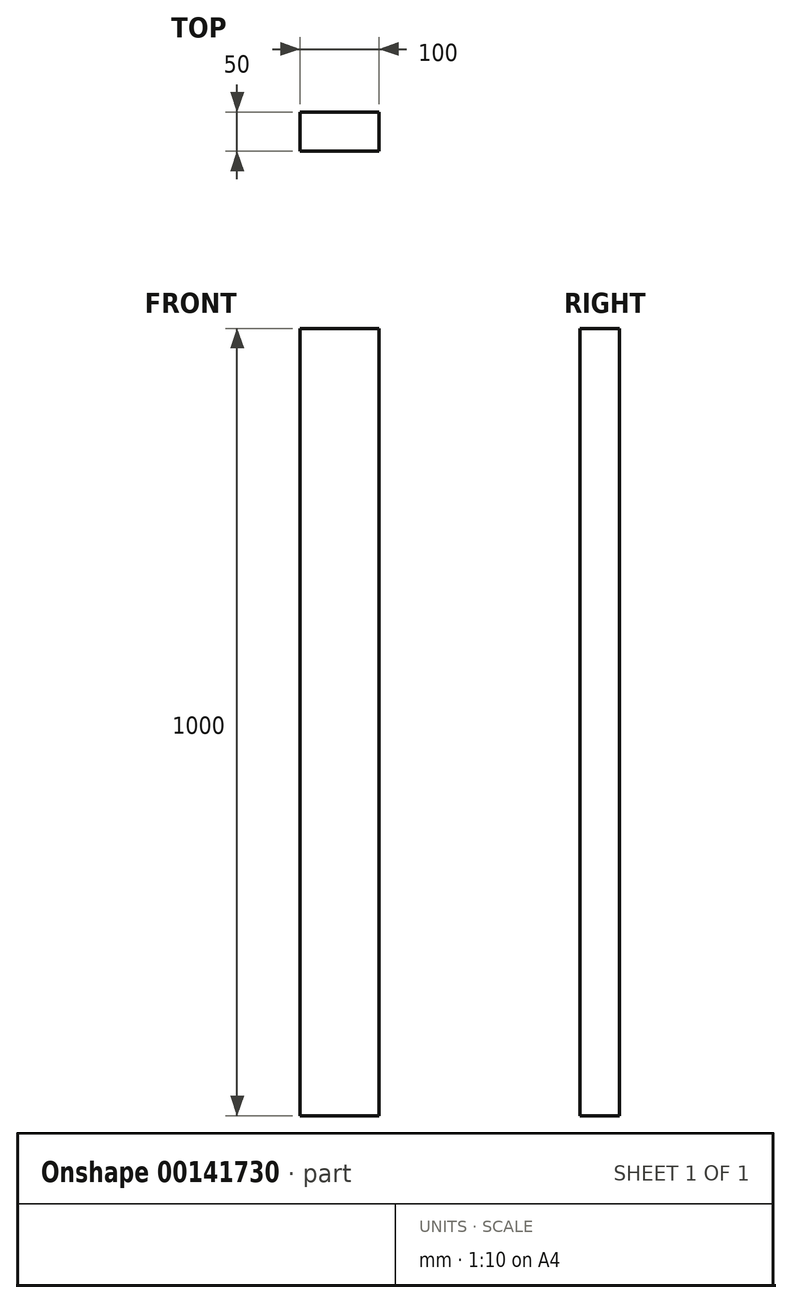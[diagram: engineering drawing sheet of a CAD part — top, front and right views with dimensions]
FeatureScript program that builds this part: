
annotation { "Feature Type Name" : "Feature", "Feature Type Description" : "" }
export const myFeature = defineFeature(function(context is Context, id is Id, definition is map)
    precondition{}
    {
        {
            var Q0;
            Q0=qCreatedBy(makeId("Top.planeOp"),FACE);
            var sketch = newSketch(context, id + "F0", { "sketchPlane" : qUnion([Q0])});
            skLineSegment(sketch, "E0.bottom", {"start": v(50, -25) * mm, "end": v(-50, -25) * mm});
            skLineSegment(sketch, "E0.top", {"start": v(50, 25) * mm, "end": v(-50, 25) * mm});
            skLineSegment(sketch, "E0.left", {"start": v(50, -25) * mm, "end": v(50, 25) * mm});
            skLineSegment(sketch, "E0.right", {"start": v(-50, -25) * mm, "end": v(-50, 25) * mm});
            skPoint(sketch, "E0.middle", {"position": v(0, 0) * mm});
            skSolve(sketch);
        }
        {
            var Q0;
            Q0=makeQuery(id+"F0.imprint","IMPRINT",FACE,{"disambiguationData":[TD([[makeQuery(id+"F0.imprint","IMPRINT",EDGE,{"derivedFrom":sQuery(id+"F0.wireOp",EDGE,"E0.bottom")}),-1.0]])]});
            extrude(context, id + "F1", {"entities" : qUnion([Q0]), "depth" : 1000 * mm});
        }
    });
